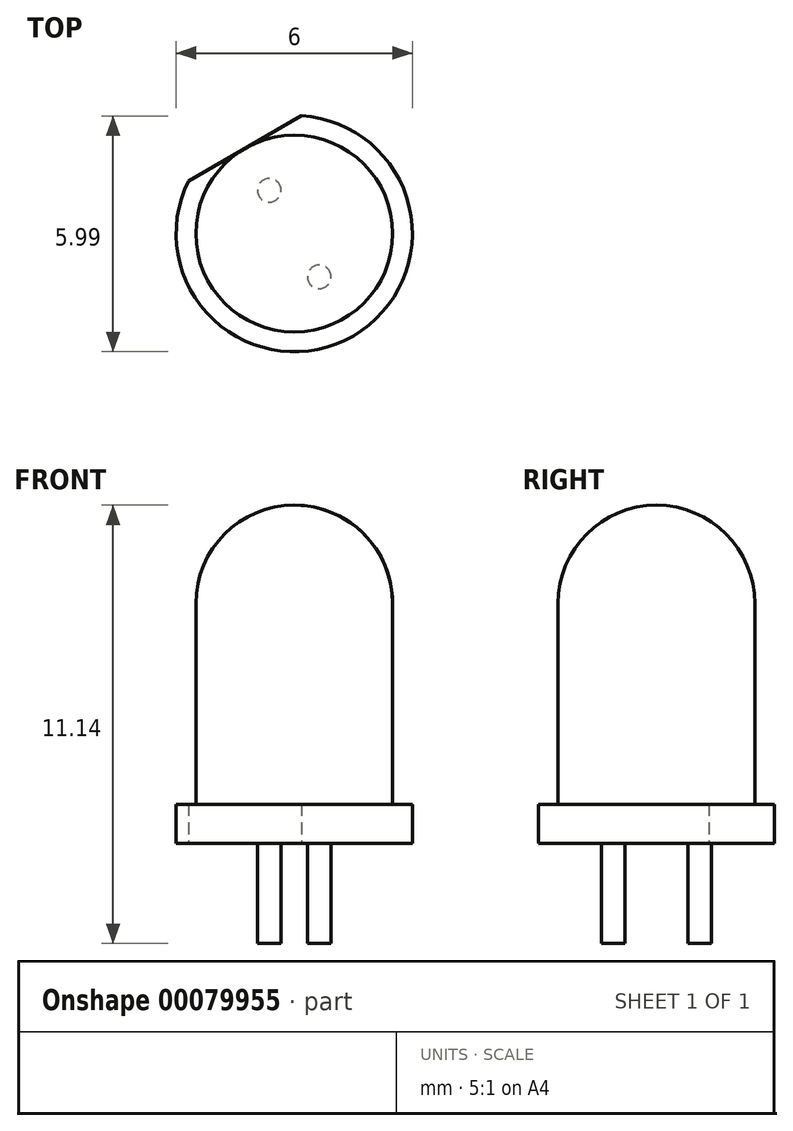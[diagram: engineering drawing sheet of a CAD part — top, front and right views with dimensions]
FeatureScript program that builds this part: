
annotation { "Feature Type Name" : "Feature", "Feature Type Description" : "" }
export const myFeature = defineFeature(function(context is Context, id is Id, definition is map)
    precondition{}
    {
        {
            var Q0;
            Q0=qCreatedBy(makeId("Top.planeOp"),FACE);
            var sketch = newSketch(context, id + "F0", { "sketchPlane" : qUnion([Q0])});
            skCircle(sketch, "E0", {"center": v(0, 0) * mm, "radius": 2.5 * mm});
            skCircle(sketch, "E1", {"center": v(0, 0) * mm, "radius": 3 * mm});
            skLineSegment(sketch, "E2", {"start": v(-1.27, 0) * mm, "end": v(1.27, 0) * mm});
            skCircle(sketch, "E3", {"center": v(-1.27, 0) * mm, "radius": 0.3 * mm});
            skCircle(sketch, "E4", {"center": v(1.27, 0) * mm, "radius": 0.3 * mm});
            skLineSegment(sketch, "E5", {"start": v(2.5, -1.66) * mm, "end": v(2.5, 1.66) * mm});
            skLineSegment(sketch, "E6", {"start": v(-2.69, -1.34) * mm, "end": v(0.18, -3) * mm});
            skLineSegment(sketch, "E7", {"start": v(-2.69, 1.34) * mm, "end": v(0.18, 3) * mm});
            skCircle(sketch, "E8", {"center": v(-0.64, -1.1) * mm, "radius": 0.3 * mm});
            skCircle(sketch, "E9", {"center": v(0.64, -1.1) * mm, "radius": 0.3 * mm});
            skCircle(sketch, "E10", {"center": v(0.64, 1.1) * mm, "radius": 0.3 * mm});
            skCircle(sketch, "E11", {"center": v(-0.64, 1.1) * mm, "radius": 0.3 * mm});
            skLineSegment(sketch, "E12", {"start": v(-0.64, -1.1) * mm, "end": v(-1.27, 0) * mm});
            skLineSegment(sketch, "E13", {"start": v(-0.64, -1.1) * mm, "end": v(0.64, -1.1) * mm});
            skLineSegment(sketch, "E14", {"start": v(0.63, -1.1) * mm, "end": v(1.27, 0) * mm});
            skLineSegment(sketch, "E15", {"start": v(1.27, 0) * mm, "end": v(0.63, 1.1) * mm});
            skLineSegment(sketch, "E16", {"start": v(-0.64, 1.1) * mm, "end": v(0.64, 1.1) * mm});
            skLineSegment(sketch, "E17", {"start": v(-0.64, 1.1) * mm, "end": v(-1.27, 0) * mm});
            skLineSegment(sketch, "E18", {"start": v(-0.64, -1.1) * mm, "end": v(0.64, 1.1) * mm});
            skLineSegment(sketch, "E19", {"start": v(-0.63, 1.1) * mm, "end": v(0.63, -1.1) * mm});
            skSolve(sketch);
        }
        {
            var Q0;
            Q0=makeQuery(id+"F0.imprint","IMPRINT",FACE,{"disambiguationData":[TD([[makeQuery(id+"F0.imprint","IMPRINT",EDGE,{"derivedFrom":sQuery(id+"F0.wireOp",EDGE,"E0")}),1.0]])]});
            var Q1;
            Q1=makeQuery(id+"F0.imprint","IMPRINT",FACE,{"disambiguationData":[TD([[makeQuery(id+"F0.imprint","IMPRINT",EDGE,{"derivedFrom":sQuery(id+"F0.wireOp",EDGE,"E3")}),1.0]])]});
            var Q2;
            Q2=makeQuery(id+"F0.imprint","IMPRINT",FACE,{"disambiguationData":[TD([[makeQuery(id+"F0.imprint","IMPRINT",EDGE,{"derivedFrom":sQuery(id+"F0.wireOp",EDGE,"E4")}),1.0]])]});
            var Q3;
            {var subQ5=sQuery(id+"F0.wireOp",EDGE,"E18");var subQ6=sQuery(id+"F0.wireOp",EDGE,"E8");var subQ7=makeQuery(id+"F0.imprint","INTERSECT",VERTEX,{"derivedFrom":[subQ6,subQ5]});Q3=makeQuery(id+"F0.imprint","IMPRINT",FACE,{"disambiguationData":[TD([[makeQuery(id+"F0.imprint","IMPRINT",EDGE,{"disambiguationData":[TD([[subQ7,1.0]])],"derivedFrom":subQ6}),-1.0]])]});}
            var Q4;
            {var subQ1=sQuery(id+"F0.wireOp",EDGE,"E3");var subQ7=sQuery(id+"F0.wireOp",EDGE,"E2");var subQ8=makeQuery(id+"F0.imprint","INTERSECT",VERTEX,{"derivedFrom":[subQ7,subQ1]});Q4=makeQuery(id+"F0.imprint","IMPRINT",FACE,{"disambiguationData":[TD([[makeQuery(id+"F0.imprint","IMPRINT",EDGE,{"disambiguationData":[TD([[subQ8,1.0]])],"derivedFrom":subQ1}),-1.0]])]});}
            var Q5;
            {var subQ0=sQuery(id+"F0.wireOp",EDGE,"E18");var subQ1=sQuery(id+"F0.wireOp",EDGE,"E8");var subQ2=makeQuery(id+"F0.imprint","INTERSECT",VERTEX,{"derivedFrom":[subQ1,subQ0]});Q5=makeQuery(id+"F0.imprint","IMPRINT",FACE,{"disambiguationData":[TD([[makeQuery(id+"F0.imprint","IMPRINT",EDGE,{"disambiguationData":[TD([[subQ2,-1.0]])],"derivedFrom":subQ1}),1.0]])]});}
            var Q6;
            {var subQ0=sQuery(id+"F0.wireOp",EDGE,"E18");var subQ1=sQuery(id+"F0.wireOp",EDGE,"E8");var subQ2=makeQuery(id+"F0.imprint","INTERSECT",VERTEX,{"derivedFrom":[subQ1,subQ0]});Q6=makeQuery(id+"F0.imprint","IMPRINT",FACE,{"disambiguationData":[TD([[makeQuery(id+"F0.imprint","IMPRINT",EDGE,{"disambiguationData":[TD([[subQ2,1.0]])],"derivedFrom":subQ1}),1.0]])]});}
            var Q7;
            {var subQ0=sQuery(id+"F0.wireOp",EDGE,"E13");var subQ1=sQuery(id+"F0.wireOp",EDGE,"E8");var subQ2=makeQuery(id+"F0.imprint","INTERSECT",VERTEX,{"derivedFrom":[subQ1,subQ0]});Q7=makeQuery(id+"F0.imprint","IMPRINT",FACE,{"disambiguationData":[TD([[makeQuery(id+"F0.imprint","IMPRINT",EDGE,{"disambiguationData":[TD([[subQ2,1.0]])],"derivedFrom":subQ1}),1.0]])]});}
            var Q8;
            {var subQ1=sQuery(id+"F0.wireOp",EDGE,"E4");var subQ7=sQuery(id+"F0.wireOp",EDGE,"E2");var subQ9=makeQuery(id+"F0.imprint","INTERSECT",VERTEX,{"derivedFrom":[subQ7,subQ1]});Q8=makeQuery(id+"F0.imprint","IMPRINT",FACE,{"disambiguationData":[TD([[makeQuery(id+"F0.imprint","IMPRINT",EDGE,{"disambiguationData":[TD([[subQ9,-1.0]])],"derivedFrom":subQ1}),-1.0]])]});}
            var Q9;
            {var subQ0=sQuery(id+"F0.wireOp",EDGE,"E19");var subQ1=sQuery(id+"F0.wireOp",EDGE,"E9");var subQ2=makeQuery(id+"F0.imprint","INTERSECT",VERTEX,{"derivedFrom":[subQ1,subQ0]});Q9=makeQuery(id+"F0.imprint","IMPRINT",FACE,{"disambiguationData":[TD([[makeQuery(id+"F0.imprint","IMPRINT",EDGE,{"disambiguationData":[TD([[subQ2,1.0]])],"derivedFrom":subQ1}),1.0]])]});}
            var Q10;
            {var subQ0=sQuery(id+"F0.wireOp",EDGE,"E19");var subQ1=sQuery(id+"F0.wireOp",EDGE,"E9");var subQ2=makeQuery(id+"F0.imprint","INTERSECT",VERTEX,{"derivedFrom":[subQ1,subQ0]});Q10=makeQuery(id+"F0.imprint","IMPRINT",FACE,{"disambiguationData":[TD([[makeQuery(id+"F0.imprint","IMPRINT",EDGE,{"disambiguationData":[TD([[subQ2,-1.0]])],"derivedFrom":subQ1}),1.0]])]});}
            var Q11;
            {var subQ0=sQuery(id+"F0.wireOp",EDGE,"E14");var subQ1=sQuery(id+"F0.wireOp",EDGE,"E9");var subQ2=makeQuery(id+"F0.imprint","INTERSECT",VERTEX,{"derivedFrom":[subQ1,subQ0]});Q11=makeQuery(id+"F0.imprint","IMPRINT",FACE,{"disambiguationData":[TD([[makeQuery(id+"F0.imprint","IMPRINT",EDGE,{"disambiguationData":[TD([[subQ2,1.0]])],"derivedFrom":subQ1}),1.0]])]});}
            var Q12;
            {var subQ1=sQuery(id+"F0.wireOp",EDGE,"E4");var subQ7=sQuery(id+"F0.wireOp",EDGE,"E2");var subQ8=makeQuery(id+"F0.imprint","INTERSECT",VERTEX,{"derivedFrom":[subQ7,subQ1]});Q12=makeQuery(id+"F0.imprint","IMPRINT",FACE,{"disambiguationData":[TD([[makeQuery(id+"F0.imprint","IMPRINT",EDGE,{"disambiguationData":[TD([[subQ8,1.0]])],"derivedFrom":subQ1}),-1.0]])]});}
            var Q13;
            {var subQ0=sQuery(id+"F0.wireOp",EDGE,"E18");var subQ1=sQuery(id+"F0.wireOp",EDGE,"E10");var subQ2=makeQuery(id+"F0.imprint","INTERSECT",VERTEX,{"derivedFrom":[subQ1,subQ0]});Q13=makeQuery(id+"F0.imprint","IMPRINT",FACE,{"disambiguationData":[TD([[makeQuery(id+"F0.imprint","IMPRINT",EDGE,{"disambiguationData":[TD([[subQ2,1.0]])],"derivedFrom":subQ1}),-1.0]])]});}
            var Q14;
            {var subQ1=sQuery(id+"F0.wireOp",EDGE,"E3");var subQ7=sQuery(id+"F0.wireOp",EDGE,"E2");var subQ9=makeQuery(id+"F0.imprint","INTERSECT",VERTEX,{"derivedFrom":[subQ7,subQ1]});Q14=makeQuery(id+"F0.imprint","IMPRINT",FACE,{"disambiguationData":[TD([[makeQuery(id+"F0.imprint","IMPRINT",EDGE,{"disambiguationData":[TD([[subQ9,-1.0]])],"derivedFrom":subQ1}),-1.0]])]});}
            var Q15;
            {var subQ0=sQuery(id+"F0.wireOp",EDGE,"E17");var subQ1=sQuery(id+"F0.wireOp",EDGE,"E11");var subQ2=makeQuery(id+"F0.imprint","INTERSECT",VERTEX,{"derivedFrom":[subQ1,subQ0]});Q15=makeQuery(id+"F0.imprint","IMPRINT",FACE,{"disambiguationData":[TD([[makeQuery(id+"F0.imprint","IMPRINT",EDGE,{"disambiguationData":[TD([[subQ2,-1.0]])],"derivedFrom":subQ1}),1.0]])]});}
            var Q16;
            {var subQ0=sQuery(id+"F0.wireOp",EDGE,"E16");var subQ1=sQuery(id+"F0.wireOp",EDGE,"E11");var subQ2=makeQuery(id+"F0.imprint","INTERSECT",VERTEX,{"derivedFrom":[subQ1,subQ0]});Q16=makeQuery(id+"F0.imprint","IMPRINT",FACE,{"disambiguationData":[TD([[makeQuery(id+"F0.imprint","IMPRINT",EDGE,{"disambiguationData":[TD([[subQ2,1.0]])],"derivedFrom":subQ1}),1.0]])]});}
            var Q17;
            {var subQ0=sQuery(id+"F0.wireOp",EDGE,"E17");var subQ1=sQuery(id+"F0.wireOp",EDGE,"E11");var subQ2=makeQuery(id+"F0.imprint","INTERSECT",VERTEX,{"derivedFrom":[subQ1,subQ0]});Q17=makeQuery(id+"F0.imprint","IMPRINT",FACE,{"disambiguationData":[TD([[makeQuery(id+"F0.imprint","IMPRINT",EDGE,{"disambiguationData":[TD([[subQ2,1.0]])],"derivedFrom":subQ1}),1.0]])]});}
            var Q18;
            {var subQ0=sQuery(id+"F0.wireOp",EDGE,"E18");var subQ1=sQuery(id+"F0.wireOp",EDGE,"E10");var subQ2=makeQuery(id+"F0.imprint","INTERSECT",VERTEX,{"derivedFrom":[subQ1,subQ0]});Q18=makeQuery(id+"F0.imprint","IMPRINT",FACE,{"disambiguationData":[TD([[makeQuery(id+"F0.imprint","IMPRINT",EDGE,{"disambiguationData":[TD([[subQ2,1.0]])],"derivedFrom":subQ1}),1.0]])]});}
            var Q19;
            {var subQ0=sQuery(id+"F0.wireOp",EDGE,"E16");var subQ1=sQuery(id+"F0.wireOp",EDGE,"E10");var subQ2=makeQuery(id+"F0.imprint","INTERSECT",VERTEX,{"derivedFrom":[subQ1,subQ0]});Q19=makeQuery(id+"F0.imprint","IMPRINT",FACE,{"disambiguationData":[TD([[makeQuery(id+"F0.imprint","IMPRINT",EDGE,{"disambiguationData":[TD([[subQ2,1.0]])],"derivedFrom":subQ1}),1.0]])]});}
            var Q20;
            {var subQ0=sQuery(id+"F0.wireOp",EDGE,"E18");var subQ1=sQuery(id+"F0.wireOp",EDGE,"E10");var subQ2=makeQuery(id+"F0.imprint","INTERSECT",VERTEX,{"derivedFrom":[subQ1,subQ0]});Q20=makeQuery(id+"F0.imprint","IMPRINT",FACE,{"disambiguationData":[TD([[makeQuery(id+"F0.imprint","IMPRINT",EDGE,{"disambiguationData":[TD([[subQ2,-1.0]])],"derivedFrom":subQ1}),1.0]])]});}
            extrude(context, id + "F1", {"entities" : qUnion([Q0, Q1, Q2, Q3, Q4, Q5, Q6, Q7, Q8, Q9, Q10, Q11, Q12, Q13, Q14, Q15, Q16, Q17, Q18, Q19, Q20]), "depth" : 8.6 * mm});
        }
        {
            var Q0;
            Q0=makeQuery(id+"F1.opExtrude","CAP_EDGE",EDGE,{"disambiguationData":[OSD([sQuery(id+"F0.wireOp",EDGE,"E0")])],"isStart":false});
            fillet(context, id + "F2", {"entities" : qUnion([Q0]), "radius" : 5 * mm / 2, "tangentPropagation" : true, "allowEdgeOverflow" : false});
        }
        {
            var Q0;
            {var subQ0=sQuery(id+"F0.wireOp",EDGE,"E0");Q0=makeQuery(id+"F0.imprint","IMPRINT",FACE,{"disambiguationData":[TD([[makeQuery(id+"F0.imprint","IMPRINT",EDGE,{"derivedFrom":subQ0}),-1.0]])]});}
            var Q1;
            {var subQ0=sQuery(id+"F0.wireOp",EDGE,"E6");Q1=makeQuery(id+"F0.imprint","IMPRINT",FACE,{"disambiguationData":[TD([[makeQuery(id+"F0.imprint","IMPRINT",EDGE,{"derivedFrom":subQ0}),-1.0]])]});}
            var Q2;
            {var subQ0=sQuery(id+"F0.wireOp",EDGE,"E5");Q2=makeQuery(id+"F0.imprint","IMPRINT",FACE,{"disambiguationData":[TD([[makeQuery(id+"F0.imprint","IMPRINT",EDGE,{"derivedFrom":subQ0}),-1.0]])]});}
            extrude(context, id + "F3", {"entities" : qUnion([Q0, Q1, Q2]), "operationType" : NewBodyOperationType.ADD, "depth" : 1 * mm});
        }
        {
            var Q0;
            {var subQ0=sQuery(id+"F0.wireOp",EDGE,"E16");var subQ1=sQuery(id+"F0.wireOp",EDGE,"E11");var subQ2=makeQuery(id+"F0.imprint","INTERSECT",VERTEX,{"derivedFrom":[subQ1,subQ0]});Q0=makeQuery(id+"F0.imprint","IMPRINT",FACE,{"disambiguationData":[TD([[makeQuery(id+"F0.imprint","IMPRINT",EDGE,{"disambiguationData":[TD([[subQ2,1.0]])],"derivedFrom":subQ1}),1.0]])]});}
            var Q1;
            {var subQ0=sQuery(id+"F0.wireOp",EDGE,"E17");var subQ1=sQuery(id+"F0.wireOp",EDGE,"E11");var subQ2=makeQuery(id+"F0.imprint","INTERSECT",VERTEX,{"derivedFrom":[subQ1,subQ0]});Q1=makeQuery(id+"F0.imprint","IMPRINT",FACE,{"disambiguationData":[TD([[makeQuery(id+"F0.imprint","IMPRINT",EDGE,{"disambiguationData":[TD([[subQ2,-1.0]])],"derivedFrom":subQ1}),1.0]])]});}
            var Q2;
            {var subQ0=sQuery(id+"F0.wireOp",EDGE,"E17");var subQ1=sQuery(id+"F0.wireOp",EDGE,"E11");var subQ2=makeQuery(id+"F0.imprint","INTERSECT",VERTEX,{"derivedFrom":[subQ1,subQ0]});Q2=makeQuery(id+"F0.imprint","IMPRINT",FACE,{"disambiguationData":[TD([[makeQuery(id+"F0.imprint","IMPRINT",EDGE,{"disambiguationData":[TD([[subQ2,1.0]])],"derivedFrom":subQ1}),1.0]])]});}
            extrude(context, id + "F4", {"entities" : qUnion([Q0, Q1, Q2]), "operationType" : NewBodyOperationType.ADD, "oppositeDirection" : true, "depth" : 2.54 * mm});
        }
        {
            var Q0;
            {var subQ0=sQuery(id+"F0.wireOp",EDGE,"E19");var subQ1=sQuery(id+"F0.wireOp",EDGE,"E9");var subQ2=makeQuery(id+"F0.imprint","INTERSECT",VERTEX,{"derivedFrom":[subQ1,subQ0]});Q0=makeQuery(id+"F0.imprint","IMPRINT",FACE,{"disambiguationData":[TD([[makeQuery(id+"F0.imprint","IMPRINT",EDGE,{"disambiguationData":[TD([[subQ2,-1.0]])],"derivedFrom":subQ1}),1.0]])]});}
            var Q1;
            {var subQ0=sQuery(id+"F0.wireOp",EDGE,"E19");var subQ1=sQuery(id+"F0.wireOp",EDGE,"E9");var subQ2=makeQuery(id+"F0.imprint","INTERSECT",VERTEX,{"derivedFrom":[subQ1,subQ0]});Q1=makeQuery(id+"F0.imprint","IMPRINT",FACE,{"disambiguationData":[TD([[makeQuery(id+"F0.imprint","IMPRINT",EDGE,{"disambiguationData":[TD([[subQ2,1.0]])],"derivedFrom":subQ1}),1.0]])]});}
            var Q2;
            {var subQ0=sQuery(id+"F0.wireOp",EDGE,"E14");var subQ1=sQuery(id+"F0.wireOp",EDGE,"E9");var subQ2=makeQuery(id+"F0.imprint","INTERSECT",VERTEX,{"derivedFrom":[subQ1,subQ0]});Q2=makeQuery(id+"F0.imprint","IMPRINT",FACE,{"disambiguationData":[TD([[makeQuery(id+"F0.imprint","IMPRINT",EDGE,{"disambiguationData":[TD([[subQ2,1.0]])],"derivedFrom":subQ1}),1.0]])]});}
            extrude(context, id + "F5", {"entities" : qUnion([Q0, Q1, Q2]), "operationType" : NewBodyOperationType.ADD, "oppositeDirection" : true, "depth" : 2.54 * mm});
        }
    });
